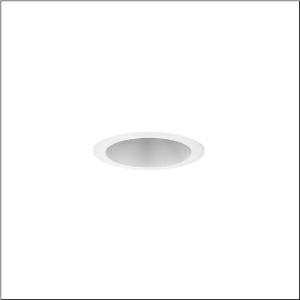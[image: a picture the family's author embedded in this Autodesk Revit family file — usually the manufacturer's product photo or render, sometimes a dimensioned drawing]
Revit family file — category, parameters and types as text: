
# Revit family: lunis_31_mini_51dn167e31
name_source: partatom
category: Lighting Fixtures
units: mm (PartAtom-declared; Revit-internal decimal feet)

## family parameters
Cut with Voids When Loaded = No
Host = Face
Light Source = No
Part Type = Normal
Room Calculation Point = No
Round Connector Dimension = Use Diameter
Shared = No

## types (1)
- Lunis 31 mini (1 x LED, 1000 lm, 8.3 W, 3000K)
    Apparent Load = 8 VA
    CIE Flux Codes = 69 93 99 100 100
    Color Rendering = 80
    Color Temperature = 3000K
    Default Elevation = 1800 mm
    Description = Lunis 31,  mini, downlight, light control with reflector, light emission: direct distribution, LED rated luminous flux: 1.000lm, light colour: 830, mains connection: 220..240V, AC, 50/60Hz, housing, white, protection rating (complete): IP20, protection rating (on room side): IP54, insulation class (complete): insulation class II (safety insulation), certification: CE, packaging unit: 1 piece
    Height = 0 mm  [stored 0 ft]
    Lamp = 1 x LED
    Lamp Light Flux = 1000 lm
    Lamp Power = 8.3 W
    Lamp count = 1
    Length = 188 mm  [stored 0.616798 ft]
    Luminous efficacy = 120 lm/W
    Manufacturer = Siteco
    ModVariant = No
    Model = 51DN167E31
    Mounting Place = Ceiling
    Mounting Type = Recessed
    Number of Poles = 1
    OnlyDefault = Yes
    Power Factor = 1
    Product Name = Lunis 31 mini
    Product group = downlight
    ProductGroupID = 400
    Protection Class = Protection class II
    Protection Degree = IP 20
    RLX_Detail_Level = 1
    RLX_Emergency_Light_Flux = 0 lm
    RLX_Emergency_Type = 0
    RLX_Emergency_Type_DB = No
    RlxData = <blob elided: 21753 chars, md5=8d04c708>
    Socket = socket
    Standby Power = 0 W
    System Light Flux = 1000 lm
    System Power = 8 W
    Type Comments = Product without accessories
    Type Image = l_1005624.jpg
    URL = http://relux.com
    VarID = ---
    Voltage = 0 V
    Weight = 0.00 kg
    Width = 0 mm  [stored 0 ft]

note: [stored X ft] marks values corroborated as IEEE doubles in the binary element streams (Revit-internal decimal feet)

## geometry (parser evidence)
native form markers: Blend x4, Sweep x10
no freeform markers — native parametric forms only
